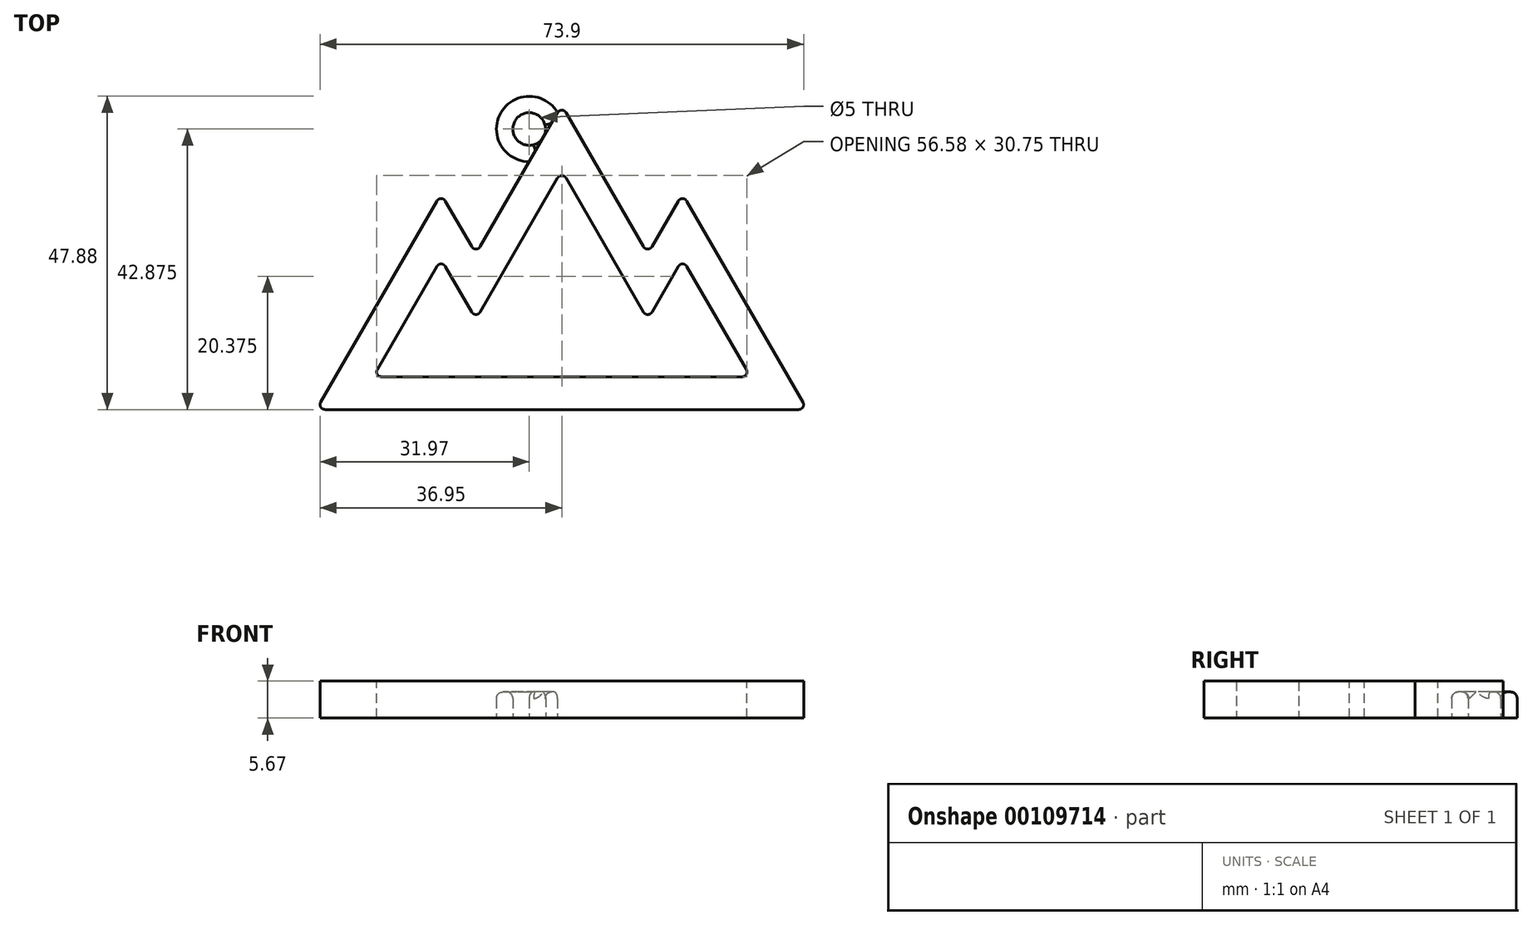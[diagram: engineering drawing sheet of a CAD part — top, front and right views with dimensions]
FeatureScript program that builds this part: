
annotation { "Feature Type Name" : "Feature", "Feature Type Description" : "" }
export const myFeature = defineFeature(function(context is Context, id is Id, definition is map)
    precondition{}
    {
        {
            var Q0;
            Q0=qCreatedBy(makeId("Top.planeOp"),FACE);
            var sketch = newSketch(context, id + "F0", { "sketchPlane" : qUnion([Q0])});
            skLineSegment(sketch, "E0", {"start": v(-37.5, 0) * mm, "end": v(37.5, 0) * mm});
            skLineSegment(sketch, "E1", {"start": v(37.5, 0) * mm, "end": v(18.45, 33) * mm});
            skLineSegment(sketch, "E2", {"start": v(18.45, 33) * mm, "end": v(13.12, 23.77) * mm});
            skLineSegment(sketch, "E3", {"start": v(13.12, 23.77) * mm, "end": v(0, 46.5) * mm});
            skLineSegment(sketch, "E4", {"start": v(0, 46.5) * mm, "end": v(-13.12, 23.77) * mm});
            skLineSegment(sketch, "E5", {"start": v(-13.12, 23.77) * mm, "end": v(-18.45, 33) * mm});
            skLineSegment(sketch, "E6", {"start": v(-18.45, 33) * mm, "end": v(-37.5, 0) * mm});
            skLineSegment(sketch, "E7", {"start": v(0, 0) * mm, "end": v(0, 46.5) * mm, "construction": true});
            skLineSegment(sketch, "E8.0", {"start": v(-13.12, 13.77) * mm, "end": v(-18.45, 23) * mm});
            skLineSegment(sketch, "E8.1", {"start": v(0, 36.5) * mm, "end": v(-13.12, 13.77) * mm});
            skLineSegment(sketch, "E8.2", {"start": v(-28.84, 5) * mm, "end": v(28.84, 5) * mm});
            skLineSegment(sketch, "E8.3", {"start": v(28.84, 5) * mm, "end": v(18.45, 23) * mm});
            skLineSegment(sketch, "E8.4", {"start": v(18.45, 23) * mm, "end": v(13.12, 13.77) * mm});
            skLineSegment(sketch, "E8.5", {"start": v(-18.45, 23) * mm, "end": v(-28.84, 5) * mm});
            skLineSegment(sketch, "E8.6", {"start": v(13.12, 13.77) * mm, "end": v(0, 36.5) * mm});
            skSolve(sketch);
        }
        {
            var Q0;
            Q0=makeQuery(id+"F0.imprint","IMPRINT",FACE,{"disambiguationData":[TD([[makeQuery(id+"F0.imprint","IMPRINT",EDGE,{"derivedFrom":sQuery(id+"F0.wireOp",EDGE,"E0")}),1.0]])]});
            extrude(context, id + "F1", {"entities" : qUnion([Q0]), "depth" : 5.67 * mm});
        }
        {
            var Q0;
            Q0=makeQuery(id+"F1.opExtrude","SWEPT_EDGE",EDGE,{"disambiguationData":[OSD([sQuery(id+"F0.wireOp",EDGE,"E8.0"),sQuery(id+"F0.wireOp",EDGE,"E8.5")])]});
            var Q1;
            Q1=makeQuery(id+"F1.opExtrude","SWEPT_EDGE",EDGE,{"disambiguationData":[OSD([sQuery(id+"F0.wireOp",EDGE,"E8.1"),sQuery(id+"F0.wireOp",EDGE,"E8.6")])]});
            var Q2;
            Q2=makeQuery(id+"F1.opExtrude","SWEPT_EDGE",EDGE,{"disambiguationData":[OSD([sQuery(id+"F0.wireOp",EDGE,"E8.3"),sQuery(id+"F0.wireOp",EDGE,"E8.4")])]});
            var Q3;
            Q3=makeQuery(id+"F1.opExtrude","SWEPT_EDGE",EDGE,{"disambiguationData":[OSD([sQuery(id+"F0.wireOp",EDGE,"E8.2"),sQuery(id+"F0.wireOp",EDGE,"E8.3")])]});
            var Q4;
            Q4=makeQuery(id+"F1.opExtrude","SWEPT_EDGE",EDGE,{"disambiguationData":[OSD([sQuery(id+"F0.wireOp",EDGE,"E8.2"),sQuery(id+"F0.wireOp",EDGE,"E8.5")])]});
            var Q5;
            Q5=makeQuery(id+"F1.opExtrude","SWEPT_EDGE",EDGE,{"disambiguationData":[OSD([sQuery(id+"F0.wireOp",EDGE,"E4"),sQuery(id+"F0.wireOp",EDGE,"E5")])]});
            var Q6;
            Q6=makeQuery(id+"F1.opExtrude","SWEPT_EDGE",EDGE,{"disambiguationData":[OSD([sQuery(id+"F0.wireOp",EDGE,"E2"),sQuery(id+"F0.wireOp",EDGE,"E3")])]});
            fillet(context, id + "F2", {"entities" : qUnion([Q0, Q1, Q2, Q3, Q4, Q5, Q6]), "radius" : 0.75 * mm, "tangentPropagation" : true, "allowEdgeOverflow" : false});
        }
        {
            var Q0;
            Q0=makeQuery(id+"F1.opExtrude","SWEPT_EDGE",EDGE,{"disambiguationData":[OSD([sQuery(id+"F0.wireOp",EDGE,"E5"),sQuery(id+"F0.wireOp",EDGE,"E6")])]});
            var Q1;
            Q1=makeQuery(id+"F1.opExtrude","SWEPT_EDGE",EDGE,{"disambiguationData":[OSD([sQuery(id+"F0.wireOp",EDGE,"E3"),sQuery(id+"F0.wireOp",EDGE,"E4")])]});
            var Q2;
            Q2=makeQuery(id+"F1.opExtrude","SWEPT_EDGE",EDGE,{"disambiguationData":[OSD([sQuery(id+"F0.wireOp",EDGE,"E1"),sQuery(id+"F0.wireOp",EDGE,"E2")])]});
            var Q3;
            Q3=makeQuery(id+"F1.opExtrude","SWEPT_EDGE",EDGE,{"disambiguationData":[OSD([sQuery(id+"F0.wireOp",EDGE,"E8.0"),sQuery(id+"F0.wireOp",EDGE,"E8.1")])]});
            var Q4;
            Q4=makeQuery(id+"F1.opExtrude","SWEPT_EDGE",EDGE,{"disambiguationData":[OSD([sQuery(id+"F0.wireOp",EDGE,"E8.4"),sQuery(id+"F0.wireOp",EDGE,"E8.6")])]});
            var Q5;
            Q5=makeQuery(id+"F1.opExtrude","SWEPT_EDGE",EDGE,{"disambiguationData":[OSD([sQuery(id+"F0.wireOp",EDGE,"E0"),sQuery(id+"F0.wireOp",EDGE,"E1")])]});
            var Q6;
            Q6=makeQuery(id+"F1.opExtrude","SWEPT_EDGE",EDGE,{"disambiguationData":[OSD([sQuery(id+"F0.wireOp",EDGE,"E0"),sQuery(id+"F0.wireOp",EDGE,"E6")])]});
            fillet(context, id + "F3", {"entities" : qUnion([Q0, Q1, Q2, Q3, Q4, Q5, Q6]), "radius" : 0.75 * mm, "tangentPropagation" : true, "allowEdgeOverflow" : false});
        }
        {
            var Q0;
            Q0=qCreatedBy(makeId("Top.planeOp"),FACE);
            var sketch = newSketch(context, id + "F4", { "sketchPlane" : qUnion([Q0])});
            skCircle(sketch, "E9", {"center": v(-4.98, 42.88) * mm, "radius": 5 * mm});
            skCircle(sketch, "E10", {"center": v(-4.98, 42.88) * mm, "radius": 2.5 * mm});
            skSolve(sketch);
        }
        {
            var Q0;
            Q0 = qSketchRegion(id + "F4", true);
            extrude(context, id + "F5", {"entities" : qUnion([Q0]), "operationType" : NewBodyOperationType.ADD, "depth" : 4 * mm});
        }
        {
            var Q0;
            Q0=makeQuery(id+"F5.opExtrude","CAP_EDGE",EDGE,{"disambiguationData":[OSD([sQuery(id+"F4.wireOp",EDGE,"E10")])],"isStart":false});
            var Q1;
            Q1=makeQuery(id+"F5.opExtrude","CAP_EDGE",EDGE,{"disambiguationData":[OSD([sQuery(id+"F4.wireOp",EDGE,"E9")])],"isStart":false});
            fillet(context, id + "F6", {"entities" : qUnion([Q0, Q1]), "radius" : 1 * mm, "tangentPropagation" : true, "allowEdgeOverflow" : false});
        }
    });
